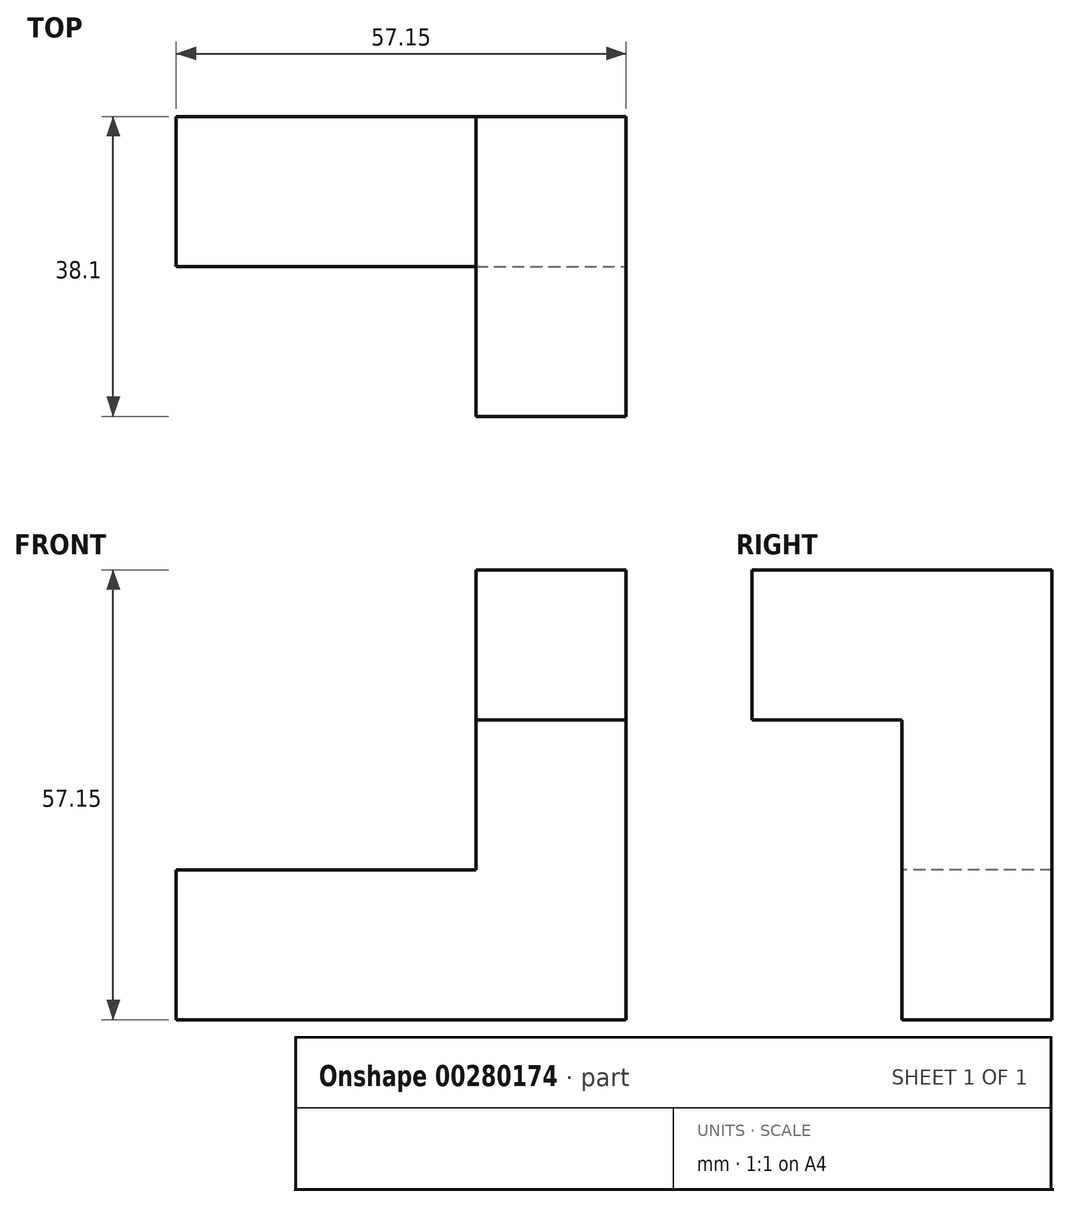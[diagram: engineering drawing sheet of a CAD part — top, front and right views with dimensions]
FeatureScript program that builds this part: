
annotation { "Feature Type Name" : "Feature", "Feature Type Description" : "" }
export const myFeature = defineFeature(function(context is Context, id is Id, definition is map)
    precondition{}
    {
        {
            var Q0;
            Q0=qCreatedBy(makeId("Top.planeOp"),FACE);
            var sketch = newSketch(context, id + "F0", { "sketchPlane" : qUnion([Q0])});
            skLineSegment(sketch, "E0.bottom", {"start": v(-66.82, 14.7) * mm, "end": v(-9.67, 14.7) * mm});
            skLineSegment(sketch, "E0.top", {"start": v(-66.82, -4.34) * mm, "end": v(-9.67, -4.34) * mm});
            skLineSegment(sketch, "E0.left", {"start": v(-66.82, 14.7) * mm, "end": v(-66.82, -4.34) * mm});
            skLineSegment(sketch, "E0.right", {"start": v(-9.67, 14.7) * mm, "end": v(-9.67, -4.34) * mm});
            skSolve(sketch);
        }
        {
            var Q0;
            Q0 = qSketchRegion(id + "F0", true);
            extrude(context, id + "F1", {"entities" : qUnion([Q0]), "depth" : 19.05 * mm});
        }
        {
            var Q0;
            Q0=makeQuery(id+"F1.opExtrude","CAP_FACE",FACE,{"disambiguationData":[OSD([sQuery(id+"F0.wireOp",EDGE,"E0.bottom"),sQuery(id+"F0.wireOp",EDGE,"E0.top"),sQuery(id+"F0.wireOp",EDGE,"E0.left"),sQuery(id+"F0.wireOp",EDGE,"E0.right")])],"isStart":false});
            var sketch = newSketch(context, id + "F2", { "sketchPlane" : qUnion([Q0])});
            skLineSegment(sketch, "E1.bottom", {"start": v(-9.67, 14.7) * mm, "end": v(-28.72, 14.7) * mm});
            skLineSegment(sketch, "E1.top", {"start": v(-9.67, -4.34) * mm, "end": v(-28.72, -4.34) * mm});
            skLineSegment(sketch, "E1.left", {"start": v(-9.67, 14.7) * mm, "end": v(-9.67, -4.34) * mm});
            skLineSegment(sketch, "E1.right", {"start": v(-28.72, 14.7) * mm, "end": v(-28.72, -4.34) * mm});
            skSolve(sketch);
        }
        {
            var Q0;
            Q0 = qSketchRegion(id + "F2", true);
            extrude(context, id + "F3", {"entities" : qUnion([Q0]), "operationType" : NewBodyOperationType.ADD, "depth" : 38.1 * mm});
        }
        {
            var Q0;
            Q0=makeQuery(id+"F3.boolean.opBoolean","MERGE",FACE,{"derivedFrom":[makeQuery(id+"F1.opExtrude","SWEPT_FACE",FACE,{"disambiguationData":[OSD([sQuery(id+"F0.wireOp",EDGE,"E0.top")])]}),makeQuery(id+"F3.opExtrude","SWEPT_FACE",FACE,{"disambiguationData":[OSD([sQuery(id+"F2.wireOp",EDGE,"E1.top")])]})]});
            var sketch = newSketch(context, id + "F4", { "sketchPlane" : qUnion([Q0])});
            skLineSegment(sketch, "E2.bottom", {"start": v(-28.72, 57.15) * mm, "end": v(-9.67, 57.15) * mm});
            skLineSegment(sketch, "E2.top", {"start": v(-28.72, 38.1) * mm, "end": v(-9.67, 38.1) * mm});
            skLineSegment(sketch, "E2.left", {"start": v(-28.72, 57.15) * mm, "end": v(-28.72, 38.1) * mm});
            skLineSegment(sketch, "E2.right", {"start": v(-9.67, 57.15) * mm, "end": v(-9.67, 38.1) * mm});
            skSolve(sketch);
        }
        {
            var Q0;
            Q0 = qSketchRegion(id + "F4", true);
            extrude(context, id + "F5", {"entities" : qUnion([Q0]), "operationType" : NewBodyOperationType.ADD, "depth" : 19.05 * mm});
        }
    });
